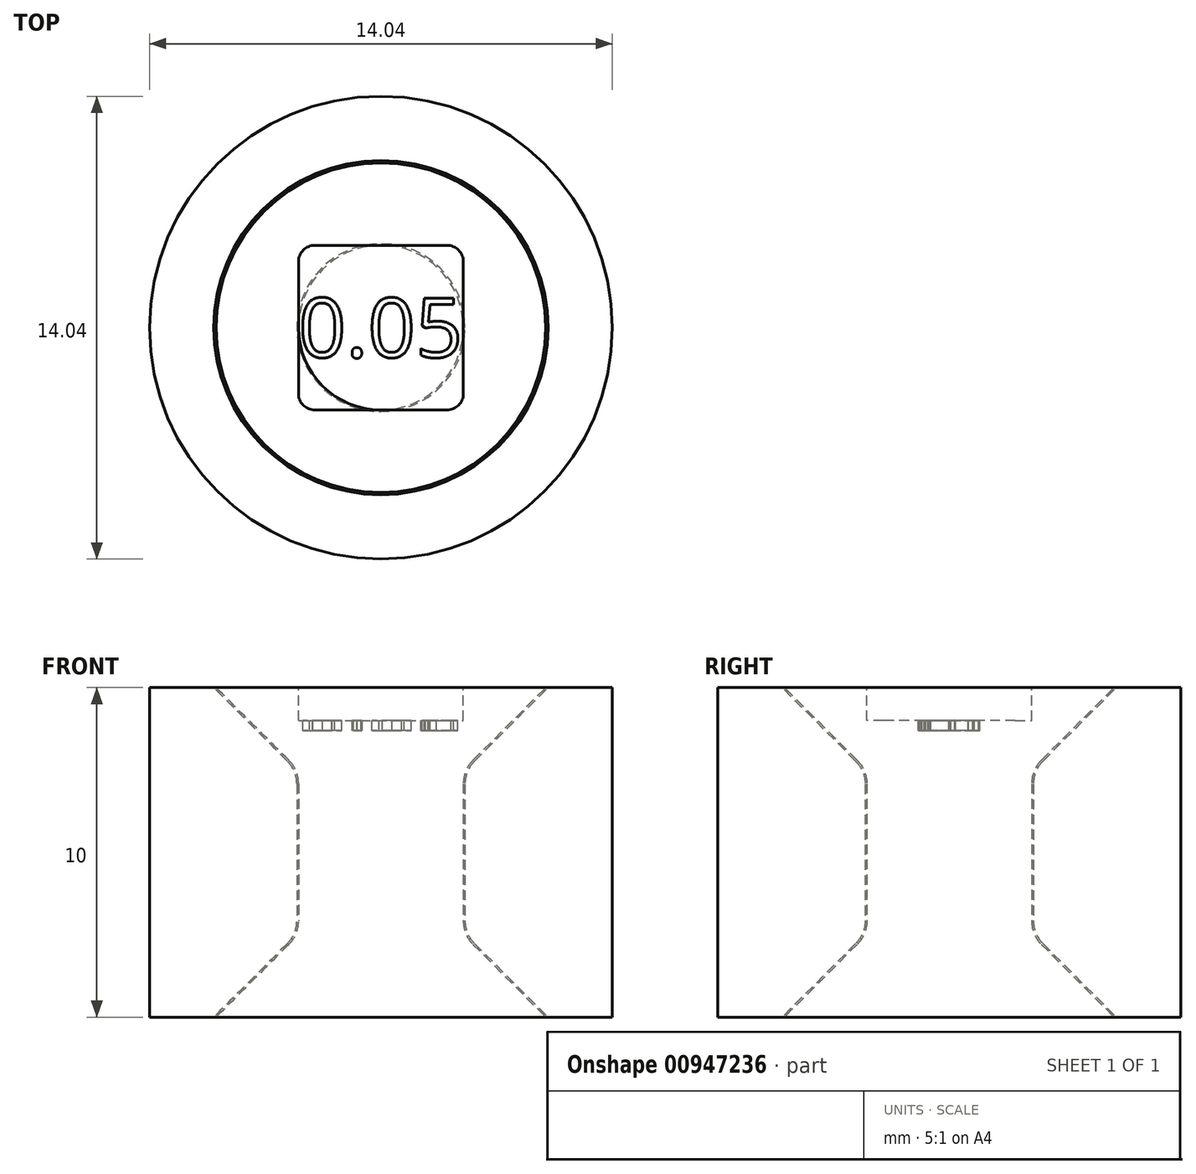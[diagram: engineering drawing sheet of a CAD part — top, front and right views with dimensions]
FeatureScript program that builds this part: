
annotation { "Feature Type Name" : "Feature", "Feature Type Description" : "" }
export const myFeature = defineFeature(function(context is Context, id is Id, definition is map)
    precondition{}
    {
        {
            var Q0;
            Q0=qCreatedBy(makeId("Front.planeOp"),FACE);
            var sketch = newSketch(context, id + "F0", { "sketchPlane" : qUnion([Q0])});
            skLineSegment(sketch, "E0", {"start": v(0, 0) * mm, "end": v(0, 10) * mm});
            skLineSegment(sketch, "E1", {"start": v(0, 10) * mm, "end": v(-5, 10) * mm});
            skLineSegment(sketch, "E2", {"start": v(-5, 10) * mm, "end": v(-2.8, 7.8) * mm});
            skLineSegment(sketch, "E3", {"start": v(-2.5, 7.09) * mm, "end": v(-2.5, 2.91) * mm});
            skLineSegment(sketch, "E4", {"start": v(-2.8, 2.2) * mm, "end": v(-5, 0) * mm});
            skLineSegment(sketch, "E5", {"start": v(-5, 0) * mm, "end": v(0, 0) * mm});
            skLineSegment(sketch, "E6", {"start": v(-7.02, 0) * mm, "end": v(-7.02, 10) * mm});
            skLineSegment(sketch, "E7", {"start": v(-7.02, 10) * mm, "end": v(-5.07, 10) * mm});
            skLineSegment(sketch, "E8", {"start": v(-5.07, 10) * mm, "end": v(-2.84, 7.77) * mm});
            skLineSegment(sketch, "E9", {"start": v(-2.55, 7.07) * mm, "end": v(-2.55, 2.93) * mm});
            skLineSegment(sketch, "E10", {"start": v(-2.84, 2.23) * mm, "end": v(-5.07, 0) * mm});
            skLineSegment(sketch, "E11", {"start": v(-5.07, 0) * mm, "end": v(-7.02, 0) * mm});
            skPoint(sketch, "E12.visualSharp", {"position": v(-2.55, 7.48) * mm});
            skArc(sketch, "E12.filletArc", {"start": v(-2.55, 7.07) * mm, "mid": v(-2.63, 7.45) * mm, "end": v(-2.84, 7.77) * mm});
            skPoint(sketch, "E13.visualSharp", {"position": v(-2.5, 7.5) * mm});
            skArc(sketch, "E13.filletArc", {"start": v(-2.5, 7.09) * mm, "mid": v(-2.58, 7.47) * mm, "end": v(-2.8, 7.8) * mm});
            skPoint(sketch, "E14.visualSharp", {"position": v(-2.55, 2.52) * mm});
            skArc(sketch, "E14.filletArc", {"start": v(-2.84, 2.23) * mm, "mid": v(-2.63, 2.55) * mm, "end": v(-2.55, 2.93) * mm});
            skPoint(sketch, "E15.visualSharp", {"position": v(-2.5, 2.5) * mm});
            skArc(sketch, "E15.filletArc", {"start": v(-2.8, 2.2) * mm, "mid": v(-2.58, 2.53) * mm, "end": v(-2.5, 2.91) * mm});
            skSolve(sketch);
        }
        {
            var Q0;
            Q0=makeQuery(id+"F0.imprint","IMPRINT",FACE,{"disambiguationData":[TD([[makeQuery(id+"F0.imprint","IMPRINT",EDGE,{"derivedFrom":sQuery(id+"F0.wireOp",EDGE,"E0")}),1.0]])]});
            var Q1;
            Q1=makeQuery(id+"F0.imprint","IMPRINT",FACE,{"disambiguationData":[TD([[makeQuery(id+"F0.imprint","IMPRINT",EDGE,{"derivedFrom":sQuery(id+"F0.wireOp",EDGE,"E6")}),-1.0]])]});
            var Q2;
            Q2=sQuery(id+"F0.wireOp",EDGE,"E0");
            revolve(context, id + "F1", {"surfaceOperationType" : NewSurfaceOperationType.NEW, "entities" : qUnion([Q0, Q1]), "axis" : qUnion([Q2]), "revolveType" : RevolveType.FULL});
        }
        {
            var Q0;
            Q0=makeQuery(id+"F1.opRevolve","SWEPT_FACE",FACE,{"disambiguationData":[OSD([sQuery(id+"F0.wireOp",EDGE,"E1")])]});
            cPlane(context, id + "F2", {"entities" : qUnion([Q0]), "cplaneType" : CPlaneType.OFFSET, "offset" : 0 * mm, "width" : 150 * mm, "height" : 150 * mm});
        }
        {
            var Q0;
            Q0=makeQuery(id+"F1.opRevolve","SWEPT_FACE",FACE,{"disambiguationData":[OSD([sQuery(id+"F0.wireOp",EDGE,"E1")])]});
            var sketch = newSketch(context, id + "F3", { "sketchPlane" : qUnion([Q0])});
            skLineSegment(sketch, "E16.bottom", {"start": v(-2, 2.5) * mm, "end": v(2, 2.5) * mm});
            skLineSegment(sketch, "E16.top", {"start": v(-2, -2.5) * mm, "end": v(2, -2.5) * mm});
            skLineSegment(sketch, "E16.left", {"start": v(-2.5, 2) * mm, "end": v(-2.5, -2) * mm});
            skLineSegment(sketch, "E16.right", {"start": v(2.5, 2) * mm, "end": v(2.5, -2) * mm});
            skPoint(sketch, "E17.visualSharp", {"position": v(-2.5, 2.5) * mm});
            skArc(sketch, "E17.filletArc", {"start": v(-2, 2.5) * mm, "mid": v(-2.35, 2.35) * mm, "end": v(-2.5, 2) * mm});
            skPoint(sketch, "E18.visualSharp", {"position": v(-2.5, -2.5) * mm});
            skArc(sketch, "E18.filletArc", {"start": v(-2.5, -2) * mm, "mid": v(-2.35, -2.35) * mm, "end": v(-2, -2.5) * mm});
            skPoint(sketch, "E19.visualSharp", {"position": v(2.5, -2.5) * mm});
            skArc(sketch, "E19.filletArc", {"start": v(2, -2.5) * mm, "mid": v(2.35, -2.35) * mm, "end": v(2.5, -2) * mm});
            skPoint(sketch, "E20.visualSharp", {"position": v(2.5, 2.5) * mm});
            skArc(sketch, "E20.filletArc", {"start": v(2.5, 2) * mm, "mid": v(2.35, 2.35) * mm, "end": v(2, 2.5) * mm});
            skPoint(sketch, "E21", {"position": v(0, 0) * mm});
            skPoint(sketch, "E22", {"position": v(-2.5, 0) * mm});
            skPoint(sketch, "E23", {"position": v(0, 2.5) * mm});
            skSolve(sketch);
        }
        {
            var Q0;
            Q0=makeQuery(id+"F3.imprint","IMPRINT",FACE,{"disambiguationData":[TD([[makeQuery(id+"F3.imprint","IMPRINT",EDGE,{"derivedFrom":sQuery(id+"F3.wireOp",EDGE,"E16.bottom")}),-1.0]])]});
            extrude(context, id + "F4", {"entities" : qUnion([Q0]), "operationType" : NewBodyOperationType.REMOVE, "oppositeDirection" : true, "depth" : 1 * mm, "offsetDistance" : 25 * mm});
        }
        {
            var Q0;
            Q0=qCreatedBy(id+"F2.planeOp",FACE);
            var sketch = newSketch(context, id + "F5", { "sketchPlane" : qUnion([Q0])});
            skText(sketch, "E24", { "text": "0.05", "fontName": "OpenSans-Regular.ttf"});
            skPoint(sketch, "E25", {"position": v(-2.5, 0) * mm});
            const initialGuessF5  = {"E24": [-0.0025, -0.0009, 1, 0, 0.00181]};
            skSetInitialGuess(sketch, initialGuessF5);
            skSolve(sketch);
        }
        {
            var Q0;
            Q0=qSketchRegion(id+"F5",true);
            extrude(context, id + "F6", {"entities" : qUnion([Q0]), "operationType" : NewBodyOperationType.REMOVE, "oppositeDirection" : true, "depth" : 1.3 * mm, "offsetDistance" : 25 * mm});
        }
    });
